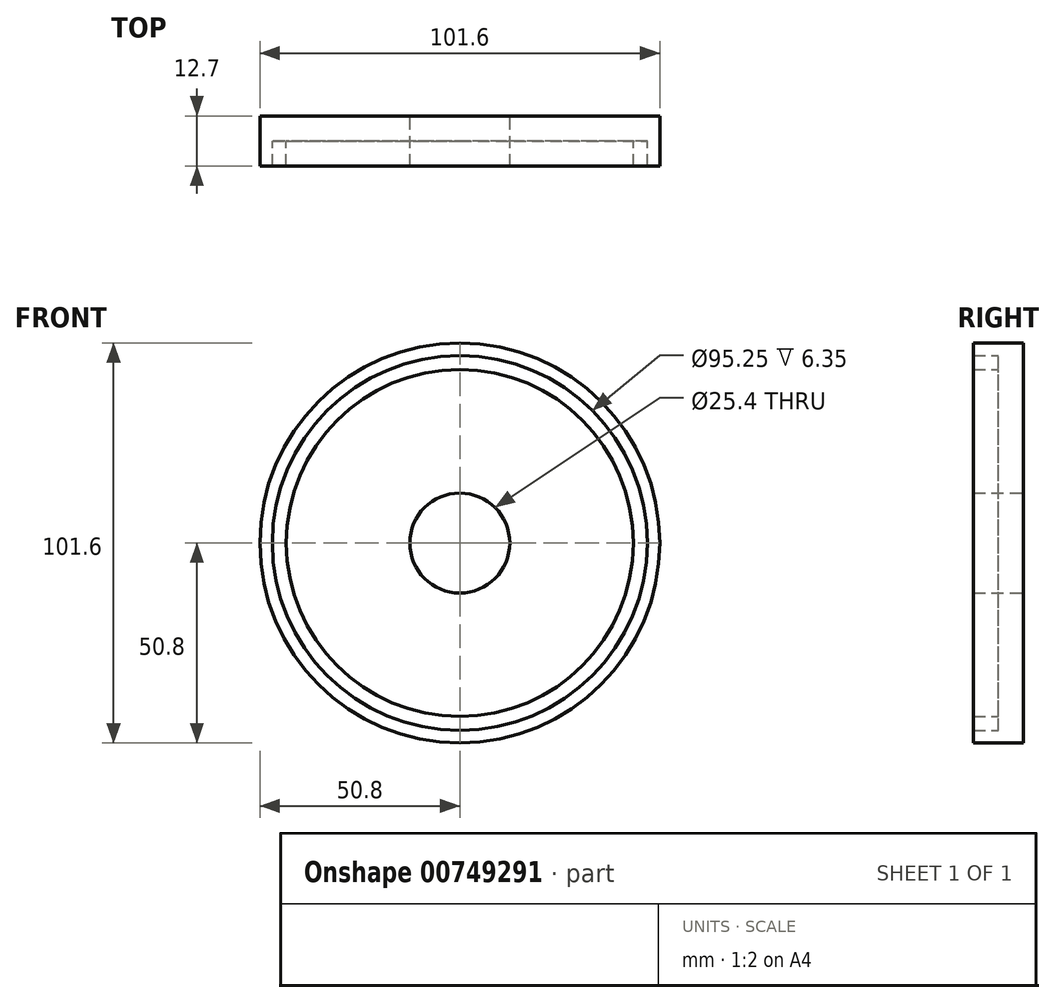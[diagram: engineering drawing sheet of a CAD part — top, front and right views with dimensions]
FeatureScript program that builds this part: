
annotation { "Feature Type Name" : "Feature", "Feature Type Description" : "" }
export const myFeature = defineFeature(function(context is Context, id is Id, definition is map)
    precondition{}
    {
        {
            var Q0;
            Q0=qCreatedBy(makeId("Front.planeOp"),FACE);
            var sketch = newSketch(context, id + "F0", { "sketchPlane" : qUnion([Q0])});
            skCircle(sketch, "E0", {"center": v(0, 0) * mm, "radius": 50.8 * mm});
            skCircle(sketch, "E1", {"center": v(0, 0) * mm, "radius": 12.7 * mm});
            skCircle(sketch, "E2", {"center": v(0, 0) * mm, "radius": 47.63 * mm});
            skCircle(sketch, "E3", {"center": v(0, 0) * mm, "radius": 44.07 * mm});
            skLineSegment(sketch, "E4", {"start": v(0, 0) * mm, "end": v(7.5, -50.24) * mm});
            skSolve(sketch);
        }
        {
            var Q0;
            Q0 = qSketchRegion(id + "F0", true);
            var Q1;
            Q1=makeQuery(id+"F0.imprint","IMPRINT",FACE,{"disambiguationData":[TD([[makeQuery(id+"F0.imprint","IMPRINT",EDGE,{"derivedFrom":sQuery(id+"F0.wireOp",EDGE,"E1")}),-1.0]])]});
            extrude(context, id + "F1", {"entities" : qUnion([Q0, Q1]), "depth" : 12.7 * mm, "offsetDistance" : 25.4 * mm});
        }
        {
            var Q0;
            Q0=makeQuery(id+"F0.imprint","IMPRINT",FACE,{"disambiguationData":[TD([[makeQuery(id+"F0.imprint","IMPRINT",EDGE,{"derivedFrom":sQuery(id+"F0.wireOp",EDGE,"E2")}),1.0]])]});
            extrude(context, id + "F2", {"entities" : qUnion([Q0]), "operationType" : NewBodyOperationType.ADD, "depth" : 6.35 * mm, "offsetDistance" : 25.4 * mm});
        }
    });
